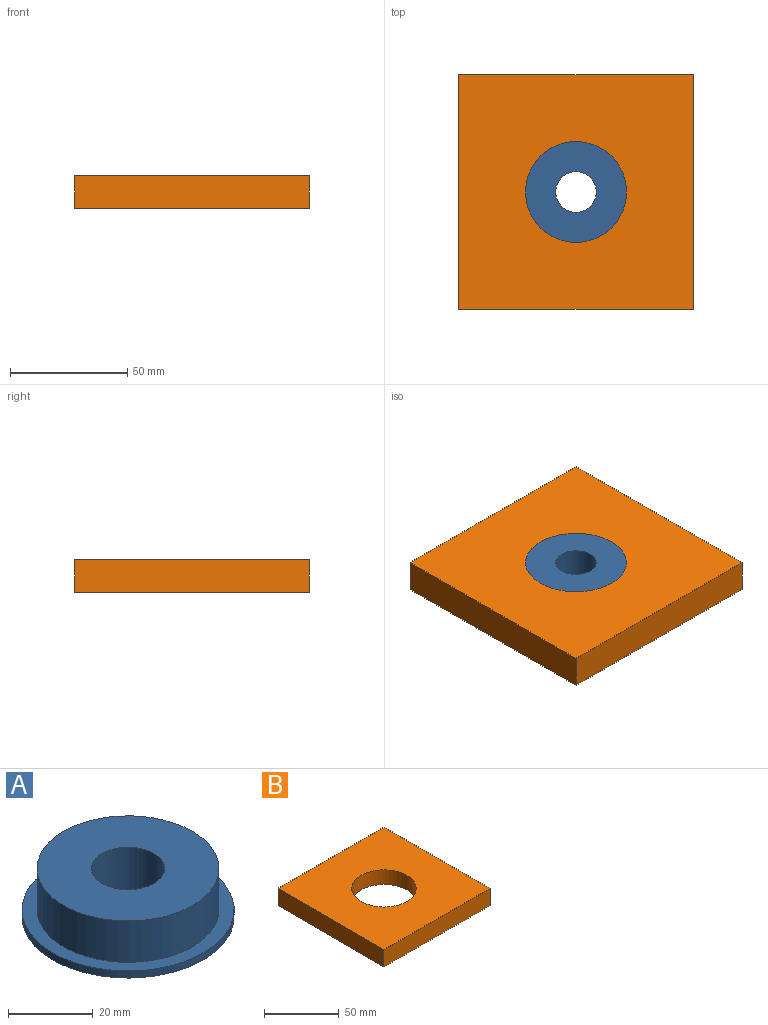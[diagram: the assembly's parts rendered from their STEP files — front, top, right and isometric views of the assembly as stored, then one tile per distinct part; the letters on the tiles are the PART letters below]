
ASSEMBLY  parts=2 mates=1
PART A: 6 faces, bbox 50.1x50.1x14 mm
  f0: cylinder r=21.5mm len=43mm, axis (0,0,-1), area 1614.3mm2, adj f1,f3
  f1: plane 43x43mm, normal (0,0,1), area 1216.3mm2, adj f0,f5
  f2: cylinder r=25.05mm len=50.1mm, axis (0,0,-1), area 322.7mm2, adj f3,f4
  f3: plane 50.1x50.1mm, normal (0,0,1), area 519.2mm2, adj f0,f2
  f4: plane 50.1x50.1mm, normal (0,0,-1), area 1735.5mm2, adj f2,f5
  f5: cylinder r=8.67mm len=17.33mm, axis (0,0,-1), area 762.2mm2, adj f1,f4
PART B: 9 faces, bbox 100x100x14 mm
  f0: plane 100x14mm, normal (1,0,0), area 1400mm2, adj f1,f3,f4,f5
  f1: plane 100x14mm, normal (0,1,0), area 1400mm2, adj f0,f2,f4,f5
  f2: plane 100x14mm, normal (-1,0,0), area 1400mm2, adj f1,f3,f4,f5
  f3: plane 100x14mm, normal (0,-1,0), area 1400mm2, adj f0,f2,f4,f5
  f4: plane 100x100mm, normal (0,0,1), area 8547.8mm2, adj f0,f1,f2,f3,f7
  f5: plane 100x100mm, normal (0,0,-1), area 8028.6mm2, adj f0,f1,f2,f3,f6
  f6: cylinder r=25.05mm len=50.1mm, axis (0,0,-1), area 322.7mm2, adj f5,f8
  f7: cylinder r=21.5mm len=43mm, axis (0,0,-1), area 1614.3mm2, adj f4,f8
  f8: plane 50.1x50.1mm, normal (0,0,-1), area 519.2mm2, adj f6,f7
PLACE A t=(-2.1,-5.75,-13.8)mm
PLACE B t=(-2.1,-5.75,-13.8)mm
MATE slider A.f2 <-> B.f6  axis (0,0,1) through (-2.1,-5.75,0.2)mm
